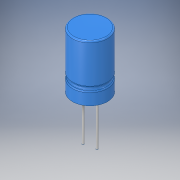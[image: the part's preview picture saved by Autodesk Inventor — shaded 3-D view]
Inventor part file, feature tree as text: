
AUTODESK INVENTOR PART (.ipt)
format: ipt  version: 2018 (Build 220112000, 112)  size: 152,064 bytes
history: native  units: in
note: dims shown in document units (in); Inventor stores cm internally (conversion verified against a paired STEP export)
features: sketch x3, extrude x2, revolve x1, fillet x1, projected_geometry x1
ambient origin geometry x8: Origin, YZ Plane, XZ Plane, XY Plane, X Axis, Y Axis, Z Axis, Center Point
bodies: Solid1 (feature_tree)
feature tree (8):
  revolve  "Revolution1"  [1 undecoded]
  fillet  "Fillet1"  Radius=0.05in
  extrude  "Extrusion1"  TaperAngle=90.0deg  [1 undecoded]
  extrude  "Extrusion2"  Depth=0.1575in
  sketch  "Sketch1"  dims[d0=0.2461in d1=0.7874in d2=0.05in]
  sketch  "Sketch2"  dims[d3=0.2in d4=90.0deg]
  sketch  "Sketch3"  dims[d5=0.02in d6=0.0236in d7=0.0236in d8=0.0984in d9=0.0984in d10=0.5906in d11=0.0in d12=0.1575in d13=0.0in]
  projected_geometry  "Projected Loop1"
note: 2 required parameter values undecoded (feature->parameter linkage not recoverable at this tier; creation-order binding heuristic only, values carry confidence <= 0.55)